annotation { "Feature Type Name" : "Feature", "Feature Type Description" : "" }
export const myFeature = defineFeature(function(context is Context, id is Id, definition is map)
    precondition{}
    {
        {
            var Q0;
            Q0=qCreatedBy(makeId("Front.planeOp"),FACE);
            var sketch = newSketch(context, id + "F0", { "sketchPlane" : qUnion([Q0])});
            skLineSegment(sketch, "E0.rect.left", {"start": v(48, 77.47) * mm, "end": v(48, -77.53) * mm});
            skLineSegment(sketch, "E0.rect.right", {"start": v(-48, 77.53) * mm, "end": v(-48, -77.47) * mm});
            skPoint(sketch, "E0.rect.middle", {"position": v(0, 0) * mm});
            skLineSegment(sketch, "E1", {"start": v(48, 77.47) * mm, "end": v(75, 77.46) * mm});
            skLineSegment(sketch, "E2", {"start": v(-48, 77.53) * mm, "end": v(-75, 77.54) * mm});
            skLineSegment(sketch, "E3.bottom", {"start": v(-75, 77.54) * mm, "end": v(-48, 77.53) * mm});
            skFitSpline(sketch, "E4", {"points": [v(-48, -77.47) * mm, v(-52.9, -82.55) * mm, v(-53.45, -92.43) * mm, v(0, -99.56) * mm], "startDerivative": vector(-26.03, -20.12) * mm, "endDerivative": vector(129.23, -0.76) * mm});
            skFitSpline(sketch, "E5.MirrorCS", {"points": [v(48, -77.47) * mm, v(52.9, -82.55) * mm, v(53.45, -92.43) * mm, v(0, -99.56) * mm], "startDerivative": vector(26.03, -20.12) * mm, "endDerivative": vector(-129.23, -0.76) * mm});
            skArc(sketch, "E6", {"start": v(75, 77.46) * mm, "mid": v(0.03, 130) * mm, "end": v(-75, 77.54) * mm});
            skLineSegment(sketch, "E7.rect.bottom", {"start": v(15, -59.83) * mm, "end": v(-15, -59.83) * mm, "construction": true});
            skLineSegment(sketch, "E7.rect.top", {"start": v(15, -89.83) * mm, "end": v(-15, -89.83) * mm, "construction": true});
            skLineSegment(sketch, "E7.rect.left", {"start": v(15, -59.83) * mm, "end": v(15, -89.83) * mm, "construction": true});
            skLineSegment(sketch, "E7.rect.right", {"start": v(-15, -59.83) * mm, "end": v(-15, -89.83) * mm, "construction": true});
            skPoint(sketch, "E7.rect.middle", {"position": v(0, -74.83) * mm});
            skLineSegment(sketch, "E8", {"start": v(-48, 77.53) * mm, "end": v(-48, 25.53) * mm});
            skLineSegment(sketch, "E9", {"start": v(-48, 25.53) * mm, "end": v(-27, 25.53) * mm, "construction": true});
            skLineSegment(sketch, "E10", {"start": v(48, 25.53) * mm, "end": v(27, 25.53) * mm, "construction": true});
            skLineSegment(sketch, "E11", {"start": v(0, 106.26) * mm, "end": v(27.5, 106.26) * mm, "construction": true});
            skLineSegment(sketch, "E12", {"start": v(0, 106.26) * mm, "end": v(-27.5, 106.26) * mm, "construction": true});
            skLineSegment(sketch, "E13.bottom", {"start": v(-25, 59.3) * mm, "end": v(-18, 59.3) * mm});
            skLineSegment(sketch, "E13.top", {"start": v(-25, 30.83) * mm, "end": v(-18, 30.83) * mm});
            skLineSegment(sketch, "E13.right", {"start": v(-18, 59.3) * mm, "end": v(-18, 30.83) * mm});
            skLineSegment(sketch, "E14", {"start": v(-25, 30.83) * mm, "end": v(-25, 59.3) * mm});
            skLineSegment(sketch, "E15.MirrorCS", {"start": v(18, 59.3) * mm, "end": v(18, 30.83) * mm});
            skLineSegment(sketch, "E16.MirrorCS", {"start": v(25, 30.83) * mm, "end": v(18, 30.83) * mm});
            skLineSegment(sketch, "E17.MirrorCS", {"start": v(25, 59.3) * mm, "end": v(18, 59.3) * mm});
            skLineSegment(sketch, "E18.MirrorCS", {"start": v(25, 30.83) * mm, "end": v(25, 59.3) * mm});
            skLineSegment(sketch, "E19", {"start": v(-35.47, 10.64) * mm, "end": v(-35.47, -35.36) * mm, "construction": true});
            skLineSegment(sketch, "E20", {"start": v(16.53, 0.13) * mm, "end": v(16.53, -24.87) * mm, "construction": true});
            skLineSegment(sketch, "E21", {"start": v(16.53, -24.87) * mm, "end": v(-35.47, -24.87) * mm, "construction": true});
            skLineSegment(sketch, "E22.rect.bottom", {"start": v(-24.6, 25.53) * mm, "end": v(-29.6, 25.53) * mm});
            skLineSegment(sketch, "E22.rect.top", {"start": v(-24.6, 16.45) * mm, "end": v(-29.6, 16.45) * mm});
            skLineSegment(sketch, "E22.rect.left", {"start": v(-24.6, 25.53) * mm, "end": v(-24.6, 16.45) * mm});
            skLineSegment(sketch, "E22.rect.right", {"start": v(-29.6, 25.53) * mm, "end": v(-29.6, 16.45) * mm});
            skLineSegment(sketch, "E23.MirrorCS", {"start": v(24.6, 25.53) * mm, "end": v(24.6, 16.45) * mm});
            skLineSegment(sketch, "E24.MirrorCS", {"start": v(24.6, 16.45) * mm, "end": v(29.6, 16.45) * mm});
            skLineSegment(sketch, "E25.MirrorCS", {"start": v(29.6, 25.53) * mm, "end": v(29.6, 16.45) * mm});
            skLineSegment(sketch, "E26", {"start": v(24.6, 25.53) * mm, "end": v(29.6, 25.53) * mm});
            skText(sketch, "E27", { "text": "Benji Bot\n", "fontName": "OpenSans-Regular.ttf"});
            skLineSegment(sketch, "E28.rect.bottom", {"start": v(8.23, 63.38) * mm, "end": v(-8.23, 63.38) * mm});
            skLineSegment(sketch, "E28.rect.top", {"start": v(8.23, 56.93) * mm, "end": v(-8.23, 56.93) * mm});
            skLineSegment(sketch, "E28.rect.left", {"start": v(8.23, 63.38) * mm, "end": v(8.23, 56.93) * mm});
            skLineSegment(sketch, "E28.rect.right", {"start": v(-8.23, 63.38) * mm, "end": v(-8.23, 56.93) * mm});
            skPoint(sketch, "E28.rect.middle", {"position": v(0, 60.15) * mm});
            skPoint(sketch, "E29.rect.middle", {"position": v(0.02, 71.08) * mm});
            skLineSegment(sketch, "E29.rect.bottom", {"start": v(8.25, 74.3) * mm, "end": v(-8.2, 74.3) * mm});
            skLineSegment(sketch, "E29.rect.right", {"start": v(-8.2, 74.3) * mm, "end": v(-8.2, 67.85) * mm});
            skLineSegment(sketch, "E29.rect.top", {"start": v(8.25, 67.85) * mm, "end": v(-8.2, 67.85) * mm});
            skLineSegment(sketch, "E29.rect.left", {"start": v(8.25, 74.3) * mm, "end": v(8.25, 67.85) * mm});
            skPoint(sketch, "E30.rect.middle", {"position": v(0.28, 81.54) * mm});
            skLineSegment(sketch, "E30.rect.bottom", {"start": v(8.51, 84.76) * mm, "end": v(-7.95, 84.76) * mm});
            skLineSegment(sketch, "E30.rect.right", {"start": v(-7.95, 84.76) * mm, "end": v(-7.95, 78.3) * mm});
            skLineSegment(sketch, "E30.rect.top", {"start": v(8.51, 78.3) * mm, "end": v(-7.95, 78.3) * mm});
            skLineSegment(sketch, "E30.rect.left", {"start": v(8.51, 84.76) * mm, "end": v(8.51, 78.3) * mm});
            skPoint(sketch, "E31.rect.middle", {"position": v(0.03, 47.82) * mm});
            skLineSegment(sketch, "E31.rect.bottom", {"start": v(8.26, 51.04) * mm, "end": v(-8.2, 51.04) * mm});
            skLineSegment(sketch, "E31.rect.right", {"start": v(-8.2, 51.04) * mm, "end": v(-8.2, 44.59) * mm});
            skLineSegment(sketch, "E31.rect.top", {"start": v(8.26, 44.59) * mm, "end": v(-8.2, 44.59) * mm});
            skLineSegment(sketch, "E31.rect.left", {"start": v(8.26, 51.04) * mm, "end": v(8.26, 44.59) * mm});
            skPoint(sketch, "E32.rect.middle", {"position": v(0.03, 36.33) * mm});
            skLineSegment(sketch, "E32.rect.bottom", {"start": v(8.26, 39.55) * mm, "end": v(-8.2, 39.55) * mm});
            skLineSegment(sketch, "E32.rect.right", {"start": v(-8.2, 39.55) * mm, "end": v(-8.2, 33.1) * mm});
            skLineSegment(sketch, "E32.rect.top", {"start": v(8.26, 33.1) * mm, "end": v(-8.2, 33.1) * mm});
            skLineSegment(sketch, "E32.rect.left", {"start": v(8.26, 39.55) * mm, "end": v(8.26, 33.1) * mm});
            const initialGuessF0  = {"E27": [-0.01745, -0.07839, 1, 0, 0.00604]};
            skSetInitialGuess(sketch, initialGuessF0);
            skSolve(sketch);
        }
        {
            var Q0;
            Q0 = qSketchRegion(id + "F0", true);
            extrude(context, id + "F1", {"entities" : qUnion([Q0]), "depth" : 3.5 * mm});
        }
        {
            var Q0;
            Q0=sQuery(id+"F0.wireOp",VERTEX,"E11.end");
            var Q1;
            Q1=sQuery(id+"F0.wireOp",VERTEX,"E12.end");
            var Q2;
            Q2=sQuery(id+"F0.wireOp",VERTEX,"E19.start");
            var Q3;
            Q3=sQuery(id+"F0.wireOp",VERTEX,"E19.end");
            var Q4;
            Q4=sQuery(id+"F0.wireOp",VERTEX,"E20.end");
            var Q5;
            Q5=sQuery(id+"F0.wireOp",VERTEX,"E20.start");
            var Q6;
            Q6=sQuery(id+"F0.wireOp",VERTEX,"E7.rect.right.start");
            var Q7;
            Q7=sQuery(id+"F0.wireOp",VERTEX,"E7.rect.bottom.start");
            var Q8;
            Q8=sQuery(id+"F0.wireOp",VERTEX,"E7.rect.top.start");
            var Q9;
            Q9=sQuery(id+"F0.wireOp",VERTEX,"E7.rect.right.end");
            var Q10;
            Q10=makeQuery(id+"F1.opExtrude","SWEPT_BODY",BODY,{"disambiguationData":[OSD([sQuery(id+"F0.wireOp",EDGE,"E0.rect.left"),sQuery(id+"F0.wireOp",EDGE,"E0.rect.right"),sQuery(id+"F0.wireOp",EDGE,"E1"),sQuery(id+"F0.wireOp",EDGE,"E3.bottom"),sQuery(id+"F0.wireOp",EDGE,"E4"),sQuery(id+"F0.wireOp",EDGE,"E5.MirrorCS"),sQuery(id+"F0.wireOp",EDGE,"E6"),sQuery(id+"F0.wireOp",EDGE,"E8"),sQuery(id+"F0.wireOp",EDGE,"E13.bottom"),sQuery(id+"F0.wireOp",EDGE,"E13.top"),sQuery(id+"F0.wireOp",EDGE,"E13.right"),sQuery(id+"F0.wireOp",EDGE,"E14"),sQuery(id+"F0.wireOp",EDGE,"E15.MirrorCS"),sQuery(id+"F0.wireOp",EDGE,"E16.MirrorCS"),sQuery(id+"F0.wireOp",EDGE,"E17.MirrorCS"),sQuery(id+"F0.wireOp",EDGE,"E18.MirrorCS")])]});
            hole(context, id + "F2", {"style" : HoleStyle.SIMPLE, "holeDiameter" : 5 * mm, "endStyle" : HoleEndStyle.THROUGH, "oppositeDirection" : true, "locations" : qUnion([Q0, Q1, Q2, Q3, Q4, Q5, Q6, Q7, Q8, Q9]), "scope" : qUnion([Q10])});
        }
    });